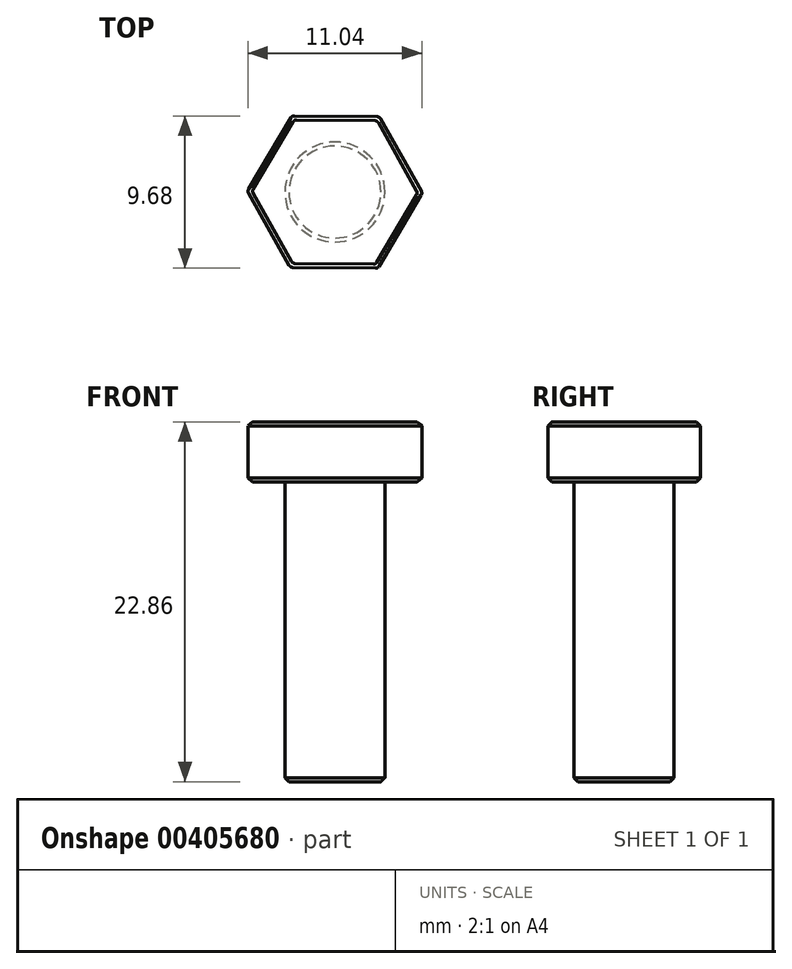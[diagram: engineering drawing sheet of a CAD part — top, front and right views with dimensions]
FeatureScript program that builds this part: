
annotation { "Feature Type Name" : "Feature", "Feature Type Description" : "" }
export const myFeature = defineFeature(function(context is Context, id is Id, definition is map)
    precondition{}
    {
        {
            var Q0;
            Q0=qCreatedBy(makeId("Front.planeOp"),FACE);
            var sketch = newSketch(context, id + "F0", { "sketchPlane" : qUnion([Q0])});
            skLineSegment(sketch, "E0.bottom", {"start": v(0, 19.05) * mm, "end": v(-3.17, 19.05) * mm});
            skLineSegment(sketch, "E0.top", {"start": v(0, 0) * mm, "end": v(-3.17, 0) * mm});
            skLineSegment(sketch, "E0.left", {"start": v(0, 19.05) * mm, "end": v(0, 0) * mm});
            skLineSegment(sketch, "E0.right", {"start": v(-3.17, 19.05) * mm, "end": v(-3.17, 0) * mm});
            skSolve(sketch);
        }
        {
            var Q0;
            Q0=makeQuery(id+"F0.imprint","IMPRINT",FACE,{"disambiguationData":[TD([[makeQuery(id+"F0.imprint","IMPRINT",EDGE,{"derivedFrom":sQuery(id+"F0.wireOp",EDGE,"E0.bottom")}),1.0]])]});
            var Q1;
            Q1=sQuery(id+"F0.wireOp",EDGE,"E0.left");
            revolve(context, id + "F1", {"entities" : qUnion([Q0]), "axis" : qUnion([Q1]), "revolveType" : RevolveType.FULL});
        }
        {
            var Q0;
            Q0=makeQuery(id+"F1.opRevolve","SWEPT_FACE",FACE,{"disambiguationData":[OSD([sQuery(id+"F0.wireOp",EDGE,"E0.bottom")])]});
            var sketch = newSketch(context, id + "F2", { "sketchPlane" : qUnion([Q0])});
            skCircle(sketch, "E1.cCircle", {"center": v(0, 0) * mm, "radius": 4.81 * mm, "construction": true});
            skLineSegment(sketch, "E1.0", {"start": v(5.56, -0.06) * mm, "end": v(2.72, -4.84) * mm});
            skLineSegment(sketch, "E1.1", {"start": v(2.72, -4.84) * mm, "end": v(-2.83, -4.78) * mm});
            skLineSegment(sketch, "E1.2", {"start": v(-2.83, -4.78) * mm, "end": v(-5.56, 0.06) * mm});
            skLineSegment(sketch, "E1.3", {"start": v(-5.56, 0.06) * mm, "end": v(-2.72, 4.84) * mm});
            skLineSegment(sketch, "E1.4", {"start": v(-2.72, 4.84) * mm, "end": v(2.83, 4.78) * mm});
            skLineSegment(sketch, "E1.5", {"start": v(2.83, 4.78) * mm, "end": v(5.56, -0.06) * mm});
            skPoint(sketch, "E1.0.midPoint", {"position": v(4.14, -2.45) * mm});
            skSolve(sketch);
        }
        {
            var Q0;
            Q0 = qSketchRegion(id + "F2", true);
            var Q1;
            Q1=sQuery(id+"F2.wireOp",EDGE,"E1.0");
            var Q2;
            Q2 = qBodyType(qCreatedBy(id + "F2" ,EDGE), BodyType.WIRE);
            extrude(context, id + "F3", {"entities" : qUnion([Q0]), "surfaceEntities" : qUnion([Q1, Q2]), "depth" : 3.8 * mm});
        }
        {
            var Q0;
            Q0=makeQuery(id+"F3.opExtrude","CAP_EDGE",EDGE,{"disambiguationData":[OSD([sQuery(id+"F2.wireOp",EDGE,"E1.3")])],"isStart":false});
            var Q1;
            Q1=makeQuery(id+"F3.opExtrude","CAP_EDGE",EDGE,{"disambiguationData":[OSD([sQuery(id+"F2.wireOp",EDGE,"E1.1")])],"isStart":false});
            var Q2;
            Q2=makeQuery(id+"F3.opExtrude","CAP_EDGE",EDGE,{"disambiguationData":[OSD([sQuery(id+"F2.wireOp",EDGE,"E1.2")])],"isStart":true});
            var Q3;
            Q3=makeQuery(id+"F3.opExtrude","CAP_EDGE",EDGE,{"disambiguationData":[OSD([sQuery(id+"F2.wireOp",EDGE,"E1.2")])],"isStart":false});
            var Q4;
            Q4=makeQuery(id+"F3.opExtrude","CAP_EDGE",EDGE,{"disambiguationData":[OSD([sQuery(id+"F2.wireOp",EDGE,"E1.4")])],"isStart":false});
            var Q5;
            Q5=makeQuery(id+"F3.opExtrude","CAP_EDGE",EDGE,{"disambiguationData":[OSD([sQuery(id+"F2.wireOp",EDGE,"E1.5")])],"isStart":false});
            var Q6;
            Q6=makeQuery(id+"F3.opExtrude","CAP_EDGE",EDGE,{"disambiguationData":[OSD([sQuery(id+"F2.wireOp",EDGE,"E1.0")])],"isStart":false});
            var Q7;
            Q7=makeQuery(id+"F3.opExtrude","CAP_EDGE",EDGE,{"disambiguationData":[OSD([sQuery(id+"F2.wireOp",EDGE,"E1.3")])],"isStart":true});
            var Q8;
            Q8=makeQuery(id+"F3.opExtrude","CAP_EDGE",EDGE,{"disambiguationData":[OSD([sQuery(id+"F2.wireOp",EDGE,"E1.4")])],"isStart":true});
            var Q9;
            Q9=makeQuery(id+"F3.opExtrude","CAP_EDGE",EDGE,{"disambiguationData":[OSD([sQuery(id+"F2.wireOp",EDGE,"E1.5")])],"isStart":true});
            var Q10;
            Q10=makeQuery(id+"F3.opExtrude","CAP_EDGE",EDGE,{"disambiguationData":[OSD([sQuery(id+"F2.wireOp",EDGE,"E1.0")])],"isStart":true});
            var Q11;
            Q11=makeQuery(id+"F3.opExtrude","CAP_EDGE",EDGE,{"disambiguationData":[OSD([sQuery(id+"F2.wireOp",EDGE,"E1.1")])],"isStart":true});
            chamfer(context, id + "F4", {"entities" : qUnion([Q0, Q1, Q2, Q3, Q4, Q5, Q6, Q7, Q8, Q9, Q10, Q11]), "width" : 0.25 * mm, "tangentPropagation" : true});
        }
        {
            var Q0;
            Q0=makeQuery(id+"F3.opExtrude","SWEPT_EDGE",EDGE,{"disambiguationData":[OSD([sQuery(id+"F2.wireOp",EDGE,"E1.1"),sQuery(id+"F2.wireOp",EDGE,"E1.2")])]});
            var Q1;
            Q1=makeQuery(id+"F3.opExtrude","SWEPT_EDGE",EDGE,{"disambiguationData":[OSD([sQuery(id+"F2.wireOp",EDGE,"E1.0"),sQuery(id+"F2.wireOp",EDGE,"E1.1")])]});
            var Q2;
            Q2=makeQuery(id+"F3.opExtrude","SWEPT_EDGE",EDGE,{"disambiguationData":[OSD([sQuery(id+"F2.wireOp",EDGE,"E1.2"),sQuery(id+"F2.wireOp",EDGE,"E1.3")])]});
            var Q3;
            Q3=makeQuery(id+"F3.opExtrude","SWEPT_EDGE",EDGE,{"disambiguationData":[OSD([sQuery(id+"F2.wireOp",EDGE,"E1.3"),sQuery(id+"F2.wireOp",EDGE,"E1.4")])]});
            var Q4;
            Q4=makeQuery(id+"F3.opExtrude","SWEPT_EDGE",EDGE,{"disambiguationData":[OSD([sQuery(id+"F2.wireOp",EDGE,"E1.4"),sQuery(id+"F2.wireOp",EDGE,"E1.5")])]});
            var Q5;
            Q5=makeQuery(id+"F3.opExtrude","SWEPT_EDGE",EDGE,{"disambiguationData":[OSD([sQuery(id+"F2.wireOp",EDGE,"E1.0"),sQuery(id+"F2.wireOp",EDGE,"E1.5")])]});
            fillet(context, id + "F5", {"entities" : qUnion([Q0, Q1, Q2, Q3, Q4, Q5]), "radius" : 0.25 * mm, "tangentPropagation" : true, "allowEdgeOverflow" : false});
        }
        {
            var Q0;
            Q0=makeQuery(id+"F4.opChamfer","BLEND_EDGE",EDGE,{"blendedFrom":[makeQuery(id+"F3.opExtrude","CAP_EDGE",EDGE,{"disambiguationData":[OSD([sQuery(id+"F2.wireOp",EDGE,"E1.2")])],"isStart":false}),makeQuery(id+"F3.opExtrude","CAP_EDGE",EDGE,{"disambiguationData":[OSD([sQuery(id+"F2.wireOp",EDGE,"E1.3")])],"isStart":false})],"blendedInto":[]});
            var Q1;
            Q1=makeQuery(id+"F4.opChamfer","BLEND_EDGE",EDGE,{"blendedFrom":[makeQuery(id+"F3.opExtrude","CAP_EDGE",EDGE,{"disambiguationData":[OSD([sQuery(id+"F2.wireOp",EDGE,"E1.3")])],"isStart":false}),makeQuery(id+"F3.opExtrude","CAP_EDGE",EDGE,{"disambiguationData":[OSD([sQuery(id+"F2.wireOp",EDGE,"E1.4")])],"isStart":false})],"blendedInto":[]});
            var Q2;
            Q2=makeQuery(id+"F4.opChamfer","BLEND_EDGE",EDGE,{"blendedFrom":[makeQuery(id+"F3.opExtrude","CAP_EDGE",EDGE,{"disambiguationData":[OSD([sQuery(id+"F2.wireOp",EDGE,"E1.4")])],"isStart":false}),makeQuery(id+"F3.opExtrude","CAP_EDGE",EDGE,{"disambiguationData":[OSD([sQuery(id+"F2.wireOp",EDGE,"E1.5")])],"isStart":false})],"blendedInto":[]});
            var Q3;
            Q3=makeQuery(id+"F4.opChamfer","BLEND_EDGE",EDGE,{"blendedFrom":[makeQuery(id+"F3.opExtrude","CAP_EDGE",EDGE,{"disambiguationData":[OSD([sQuery(id+"F2.wireOp",EDGE,"E1.0")])],"isStart":false}),makeQuery(id+"F3.opExtrude","CAP_EDGE",EDGE,{"disambiguationData":[OSD([sQuery(id+"F2.wireOp",EDGE,"E1.5")])],"isStart":false})],"blendedInto":[]});
            var Q4;
            Q4=makeQuery(id+"F4.opChamfer","BLEND_EDGE",EDGE,{"blendedFrom":[makeQuery(id+"F3.opExtrude","CAP_EDGE",EDGE,{"disambiguationData":[OSD([sQuery(id+"F2.wireOp",EDGE,"E1.0")])],"isStart":false}),makeQuery(id+"F3.opExtrude","CAP_EDGE",EDGE,{"disambiguationData":[OSD([sQuery(id+"F2.wireOp",EDGE,"E1.1")])],"isStart":false})],"blendedInto":[]});
            var Q5;
            Q5=makeQuery(id+"F4.opChamfer","BLEND_EDGE",EDGE,{"blendedFrom":[makeQuery(id+"F3.opExtrude","CAP_EDGE",EDGE,{"disambiguationData":[OSD([sQuery(id+"F2.wireOp",EDGE,"E1.1")])],"isStart":false}),makeQuery(id+"F3.opExtrude","CAP_EDGE",EDGE,{"disambiguationData":[OSD([sQuery(id+"F2.wireOp",EDGE,"E1.2")])],"isStart":false})],"blendedInto":[]});
            fillet(context, id + "F6", {"entities" : qUnion([Q0, Q1, Q2, Q3, Q4, Q5]), "radius" : 0.36 * mm, "tangentPropagation" : true, "allowEdgeOverflow" : false});
        }
        {
            var Q0;
            Q0=makeQuery(id+"F4.opChamfer","BLEND_EDGE",EDGE,{"blendedFrom":[makeQuery(id+"F3.opExtrude","CAP_EDGE",EDGE,{"disambiguationData":[OSD([sQuery(id+"F2.wireOp",EDGE,"E1.1")])],"isStart":true}),makeQuery(id+"F3.opExtrude","CAP_EDGE",EDGE,{"disambiguationData":[OSD([sQuery(id+"F2.wireOp",EDGE,"E1.2")])],"isStart":true})],"blendedInto":[]});
            var Q1;
            Q1=makeQuery(id+"F4.opChamfer","BLEND_EDGE",EDGE,{"blendedFrom":[makeQuery(id+"F3.opExtrude","CAP_EDGE",EDGE,{"disambiguationData":[OSD([sQuery(id+"F2.wireOp",EDGE,"E1.2")])],"isStart":true}),makeQuery(id+"F3.opExtrude","CAP_EDGE",EDGE,{"disambiguationData":[OSD([sQuery(id+"F2.wireOp",EDGE,"E1.3")])],"isStart":true})],"blendedInto":[]});
            var Q2;
            Q2=makeQuery(id+"F4.opChamfer","BLEND_EDGE",EDGE,{"blendedFrom":[makeQuery(id+"F3.opExtrude","CAP_EDGE",EDGE,{"disambiguationData":[OSD([sQuery(id+"F2.wireOp",EDGE,"E1.3")])],"isStart":true}),makeQuery(id+"F3.opExtrude","CAP_EDGE",EDGE,{"disambiguationData":[OSD([sQuery(id+"F2.wireOp",EDGE,"E1.4")])],"isStart":true})],"blendedInto":[]});
            var Q3;
            Q3=makeQuery(id+"F4.opChamfer","BLEND_EDGE",EDGE,{"blendedFrom":[makeQuery(id+"F3.opExtrude","CAP_EDGE",EDGE,{"disambiguationData":[OSD([sQuery(id+"F2.wireOp",EDGE,"E1.4")])],"isStart":true}),makeQuery(id+"F3.opExtrude","CAP_EDGE",EDGE,{"disambiguationData":[OSD([sQuery(id+"F2.wireOp",EDGE,"E1.5")])],"isStart":true})],"blendedInto":[]});
            var Q4;
            Q4=makeQuery(id+"F4.opChamfer","BLEND_EDGE",EDGE,{"blendedFrom":[makeQuery(id+"F3.opExtrude","CAP_EDGE",EDGE,{"disambiguationData":[OSD([sQuery(id+"F2.wireOp",EDGE,"E1.0")])],"isStart":true}),makeQuery(id+"F3.opExtrude","CAP_EDGE",EDGE,{"disambiguationData":[OSD([sQuery(id+"F2.wireOp",EDGE,"E1.5")])],"isStart":true})],"blendedInto":[]});
            var Q5;
            Q5=makeQuery(id+"F4.opChamfer","BLEND_EDGE",EDGE,{"blendedFrom":[makeQuery(id+"F3.opExtrude","CAP_EDGE",EDGE,{"disambiguationData":[OSD([sQuery(id+"F2.wireOp",EDGE,"E1.0")])],"isStart":true}),makeQuery(id+"F3.opExtrude","CAP_EDGE",EDGE,{"disambiguationData":[OSD([sQuery(id+"F2.wireOp",EDGE,"E1.1")])],"isStart":true})],"blendedInto":[]});
            fillet(context, id + "F7", {"entities" : qUnion([Q0, Q1, Q2, Q3, Q4, Q5]), "radius" : 0.36 * mm, "tangentPropagation" : true, "allowEdgeOverflow" : false});
        }
        {
            var Q0;
            Q0=makeQuery(id+"F1.opRevolve","SWEPT_FACE",FACE,{"disambiguationData":[OSD([sQuery(id+"F0.wireOp",EDGE,"E0.top")])]});
            chamfer(context, id + "F8", {"entities" : qUnion([Q0]), "width" : 0.25 * mm, "tangentPropagation" : true});
        }
    });
